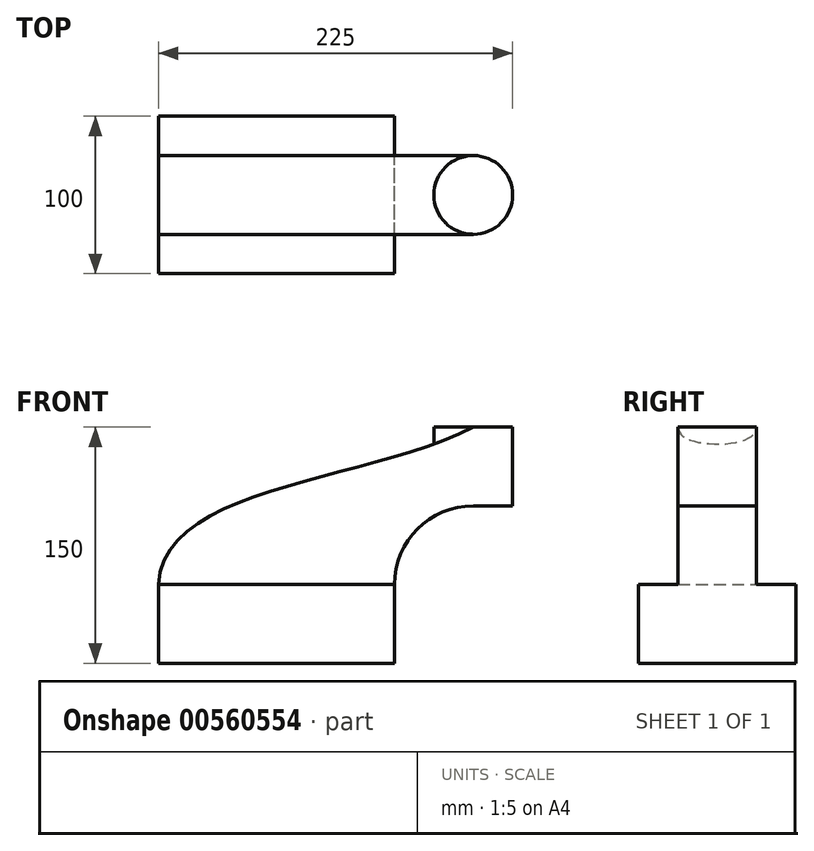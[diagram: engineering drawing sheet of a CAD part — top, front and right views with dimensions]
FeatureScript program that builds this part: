
annotation { "Feature Type Name" : "Feature", "Feature Type Description" : "" }
export const myFeature = defineFeature(function(context is Context, id is Id, definition is map)
    precondition{}
    {
        {
            var Q0;
            Q0=qCreatedBy(makeId("Front.planeOp"),FACE);
            var sketch = newSketch(context, id + "F0", { "sketchPlane" : qUnion([Q0])});
            skLineSegment(sketch, "E0.bottom", {"start": v(0, 0) * mm, "end": v(-150, 0) * mm});
            skLineSegment(sketch, "E0.top", {"start": v(0, -50) * mm, "end": v(-150, -50) * mm});
            skLineSegment(sketch, "E0.left", {"start": v(0, 0) * mm, "end": v(0, -50) * mm});
            skLineSegment(sketch, "E0.right", {"start": v(-150, 0) * mm, "end": v(-150, -50) * mm});
            skLineSegment(sketch, "E1.bottom", {"start": v(50, 100) * mm, "end": v(75, 100) * mm});
            skLineSegment(sketch, "E1.top", {"start": v(50, 50) * mm, "end": v(75, 50) * mm});
            skLineSegment(sketch, "E1.right", {"start": v(75, 100) * mm, "end": v(75, 50) * mm});
            skLineSegment(sketch, "E2", {"start": v(50, 50) * mm, "end": v(50, 100) * mm});
            skArc(sketch, "E3", {"start": v(50, 50) * mm, "mid": v(14.64, 35.36) * mm, "end": v(0, 0) * mm});
            skFitSpline(sketch, "E4", {"points": [v(-150, 0) * mm, v(50, 100) * mm], "startDerivative": vector(11.16, 191.66) * mm, "endDerivative": vector(201.79, 104.93) * mm});
            skPoint(sketch, "E5.orphan", {"position": v(25, 100) * mm});
            skPoint(sketch, "E6.orphan", {"position": v(25, 50) * mm});
            skSolve(sketch);
        }
        {
            var Q0;
            Q0=makeQuery(id+"F0.imprint","IMPRINT",FACE,{"disambiguationData":[TD([[makeQuery(id+"F0.imprint","IMPRINT",EDGE,{"derivedFrom":sQuery(id+"F0.wireOp",EDGE,"E0.bottom")}),1.0]])]});
            extrude(context, id + "F1", {"entities" : qUnion([Q0]), "endBound" : BoundingType.SYMMETRIC, "depth" : 100 * mm, "offsetDistance" : 25 * mm});
        }
        {
            var Q0;
            Q0=makeQuery(id+"F0.imprint","IMPRINT",FACE,{"disambiguationData":[TD([[makeQuery(id+"F0.imprint","IMPRINT",EDGE,{"derivedFrom":sQuery(id+"F0.wireOp",EDGE,"E0.bottom")}),-1.0]])]});
            extrude(context, id + "F2", {"entities" : qUnion([Q0]), "operationType" : NewBodyOperationType.ADD, "endBound" : BoundingType.SYMMETRIC, "depth" : 50 * mm, "offsetDistance" : 25 * mm});
        }
        {
            var Q0;
            Q0=makeQuery(id+"F0.imprint","IMPRINT",FACE,{"disambiguationData":[TD([[makeQuery(id+"F0.imprint","IMPRINT",EDGE,{"derivedFrom":sQuery(id+"F0.wireOp",EDGE,"E1.bottom")}),-1.0]])]});
            var Q1;
            Q1=sQuery(id+"F0.wireOp",EDGE,"E2");
            revolve(context, id + "F3", {"operationType" : NewBodyOperationType.ADD, "entities" : qUnion([Q0]), "axis" : qUnion([Q1]), "revolveType" : RevolveType.FULL});
        }
    });
